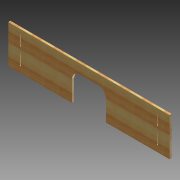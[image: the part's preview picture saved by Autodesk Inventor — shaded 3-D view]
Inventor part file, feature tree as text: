
AUTODESK INVENTOR PART (.ipt)
format: ipt  version: 2012 (Build 160160000, 160)  size: 119,808 bytes
history: native  units: in
note: dims shown in document units (in); Inventor stores cm internally (conversion verified against a paired STEP export)
features: extrude x1, sketch x1
ambient origin geometry x8: Origin, YZ Plane, XZ Plane, XY Plane, X Axis, Y Axis, Z Axis, Center Point
bodies: Solid1 (feature_tree)
feature tree (2):
  extrude  "Extrusion1"  Depth=9.0in
  sketch  "Sketch1"  dims[d0=38.0in d1=9.0in d2=0.5in d3=0.0in d4=8.0in d6=15.0in d7=6.75in d8=2.0in d9=2.75in d10=0.25in d11=2.5in d12=2.5in d13=4.0in d14=1.05in d15=0.25in d16=2.75in d17=2.5in d18=2.5in d19=4.0in d20=1.05in]
